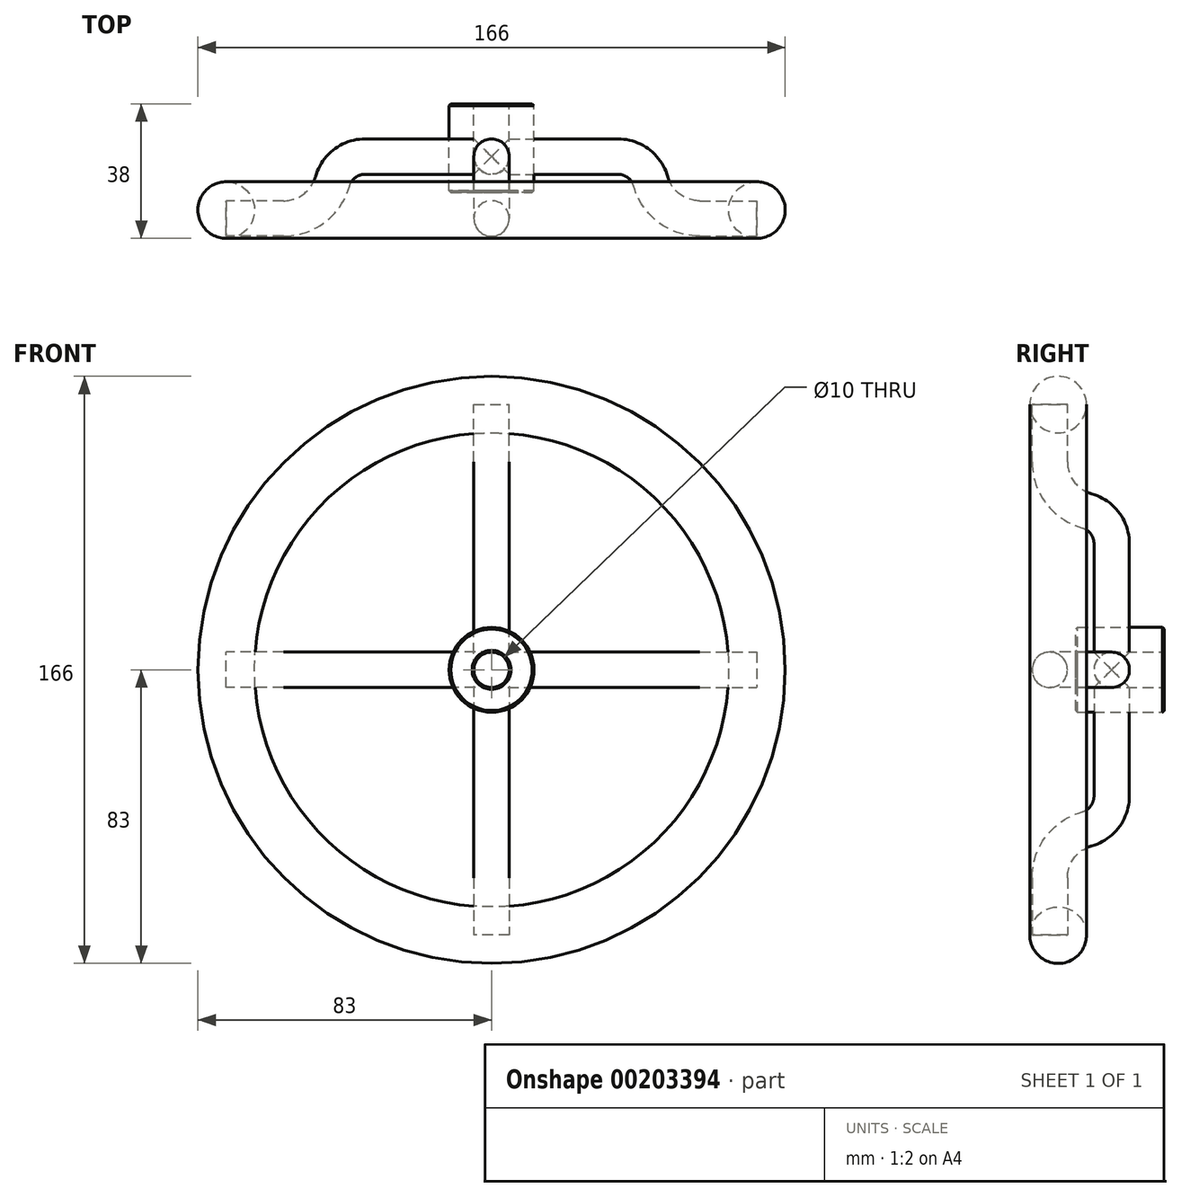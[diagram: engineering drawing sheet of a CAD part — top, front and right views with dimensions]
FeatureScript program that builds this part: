
annotation { "Feature Type Name" : "Feature", "Feature Type Description" : "" }
export const myFeature = defineFeature(function(context is Context, id is Id, definition is map)
    precondition{}
    {
        {
            var Q0;
            Q0=qCreatedBy(makeId("Front.planeOp"),FACE);
            var sketch = newSketch(context, id + "F0", { "sketchPlane" : qUnion([Q0])});
            skCircle(sketch, "E0", {"center": v(0, 0) * mm, "radius": 5 * mm});
            skCircle(sketch, "E1", {"center": v(0, 0) * mm, "radius": 12 * mm});
            skSolve(sketch);
        }
        {
            var Q0;
            Q0=makeQuery(id+"F0.imprint","IMPRINT",FACE,{"disambiguationData":[TD([[makeQuery(id+"F0.imprint","IMPRINT",EDGE,{"derivedFrom":sQuery(id+"F0.wireOp",EDGE,"E0")}),-1.0]])]});
            extrude(context, id + "F1", {"entities" : qUnion([Q0]), "depth" : 25 * mm});
        }
        {
            var Q0;
            Q0=makeQuery(id+"F1.opExtrude","CAP_FACE",FACE,{"disambiguationData":[OSD([sQuery(id+"F0.wireOp",EDGE,"E0"),sQuery(id+"F0.wireOp",EDGE,"E1")])],"isStart":false});
            var Q1;
            Q1=makeQuery(id+"F1.opExtrude","CAP_FACE",FACE,{"disambiguationData":[OSD([sQuery(id+"F0.wireOp",EDGE,"E0"),sQuery(id+"F0.wireOp",EDGE,"E1")])],"isStart":true});
            chamfer(context, id + "F2", {"entities" : qUnion([Q0, Q1]), "width" : 0.5 * mm, "tangentPropagation" : true});
        }
        {
            var Q0;
            Q0=qCreatedBy(makeId("Front.planeOp"),FACE);
            cPlane(context, id + "F3", {"entities" : qUnion([Q0]), "cplaneType" : CPlaneType.OFFSET, "offset" : 30 * mm, "width" : 150 * mm, "height" : 150 * mm});
        }
        {
            var Q0;
            Q0=qCreatedBy(makeId("Top.planeOp"),FACE);
            var sketch = newSketch(context, id + "F4", { "sketchPlane" : qUnion([Q0])});
            skCircle(sketch, "E2", {"center": v(-75, -30) * mm, "radius": 8 * mm});
            skLineSegment(sketch, "E3", {"start": v(0, 51.69) * mm, "end": v(0, -63.05) * mm});
            skLineSegment(sketch, "E4", {"start": v(-75, -30) * mm, "end": v(-58.81, -30) * mm});
            skArc(sketch, "E5", {"start": v(-58.81, -30) * mm, "mid": v(-51.57, -27.57) * mm, "end": v(-47.26, -21.25) * mm});
            skArc(sketch, "E6", {"start": v(-47.26, -21.25) * mm, "mid": v(-42.96, -14.93) * mm, "end": v(-35.71, -12.5) * mm});
            skLineSegment(sketch, "E7", {"start": v(-35.71, -12.5) * mm, "end": v(0, -12.5) * mm});
            skSolve(sketch);
        }
        {
            var Q0;
            Q0=makeQuery(id+"F4.imprint","IMPRINT",FACE,{"disambiguationData":[TD([[makeQuery(id+"F4.imprint","IMPRINT",EDGE,{"derivedFrom":sQuery(id+"F4.wireOp",EDGE,"E2")}),1.0]])]});
            var Q1;
            Q1=sQuery(id+"F4.wireOp",EDGE,"E3");
            revolve(context, id + "F5", {"entities" : qUnion([Q0]), "axis" : qUnion([Q1]), "revolveType" : RevolveType.FULL});
        }
        {
            var Q0;
            Q0=qCreatedBy(makeId("Right.planeOp"),FACE);
            var sketch = newSketch(context, id + "F6", { "sketchPlane" : qUnion([Q0])});
            skCircle(sketch, "E8", {"center": v(-14.88, 0) * mm, "radius": 5 * mm});
            skSolve(sketch);
        }
        {
            var Q0;
            Q0=makeQuery(id+"F6.imprint","IMPRINT",FACE,{"disambiguationData":[TD([[makeQuery(id+"F6.imprint","IMPRINT",EDGE,{"derivedFrom":sQuery(id+"F6.wireOp",EDGE,"E8")}),1.0]])]});
            var Q1;
            Q1=sQuery(id+"F6.wireOp",EDGE,"E8");
            var Q2;
            Q2=sQuery(id+"F4.wireOp",EDGE,"E7");
            var Q3;
            Q3=sQuery(id+"F4.wireOp",EDGE,"E6");
            var Q4;
            Q4=sQuery(id+"F4.wireOp",EDGE,"E5");
            var Q5;
            Q5=sQuery(id+"F4.wireOp",EDGE,"E4");
            sweep(context, id + "F7", {"profiles" : qUnion([Q0]), "surfaceProfiles" : qUnion([Q1]), "path" : qUnion([Q2, Q3, Q4, Q5])});
        }
        {
            var Q0;
            Q0=qCreatedBy(makeId("Top.planeOp"),FACE);
            var sketch = newSketch(context, id + "F8", { "sketchPlane" : qUnion([Q0])});
            skLineSegment(sketch, "E9", {"start": v(0, -50.24) * mm, "end": v(0, 21.2) * mm});
            skSolve(sketch);
        }
        {
            var Q0;
            Q0=makeQuery(id+"F7.opSweep","SWEPT_BODY",BODY,{"disambiguationData":[OSD([sQuery(id+"F4.wireOp",EDGE,"E4"),sQuery(id+"F6.wireOp",EDGE,"E8")])]});
            var Q1;
            Q1=sQuery(id+"F8.wireOp",EDGE,"E9");
            circularPattern(context, id + "F9", {"entities" : qUnion([Q0]), "axis" : qUnion([Q1]), "angle" : 360 * degree, "instanceCount" : 4, "equalSpace" : true});
        }
        {
            var Q0;
            Q0=makeQuery(id+"F1.opExtrude","CAP_FACE",FACE,{"disambiguationData":[OSD([sQuery(id+"F0.wireOp",EDGE,"E0"),sQuery(id+"F0.wireOp",EDGE,"E1")])],"isStart":false});
            var sketch = newSketch(context, id + "F10", { "sketchPlane" : qUnion([Q0])});
            skCircle(sketch, "E10", {"center": v(0, 0) * mm, "radius": 5 * mm});
            skSolve(sketch);
        }
        {
            var Q0;
            Q0 = qSketchRegion(id + "F10", true);
            extrude(context, id + "F11", {"entities" : qUnion([Q0]), "operationType" : NewBodyOperationType.REMOVE, "endBound" : BoundingType.SYMMETRIC, "depth" : 50 * mm});
        }
    });
